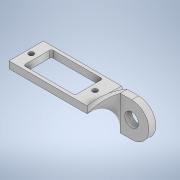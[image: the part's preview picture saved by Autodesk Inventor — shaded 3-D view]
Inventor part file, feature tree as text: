
AUTODESK INVENTOR PART (.ipt)
format: ipt  version: 2020.3 (Build 243373000, 373)  size: 189,440 bytes
history: native  units: mm
features: sketch x3, extrude x2, helix x1, plane x1, projected_geometry x1
ambient origin geometry x8: Origin, YZ Plane, XZ Plane, XY Plane, X Axis, Y Axis, Z Axis, Center Point
bodies: Body1 (feature_tree)
feature tree (8):
  extrude  "Extrusion2"  Depth=3.0mm TaperAngle=0.0deg
  helix  "Coil2"  [1 undecoded]
  plane  "Work Plane2"
  extrude  "Extrusion3"  [1 undecoded]
  sketch  "Sketch1"  dims[d30=5.0mm d31=3.0mm d32=0.0mm]
  sketch  "Sketch5"  dims[d33=40.0mm d34=10.0mm d35=2.5mm d36=0.0mm d37=90.0deg d38=90.0deg d39=0.0mm d40=0.0mm d43=3.0mm d44=0.0mm]
  projected_geometry  "Projected Loop2"
  sketch  "Sketch6"
note: 2 required parameter values undecoded (feature->parameter linkage not recoverable at this tier; creation-order binding heuristic only, values carry confidence <= 0.55)
